# Revit family: Door-Slider-Fleetwood-3070-OXIXO
name_source: partatom
category: Doors
revit_build: Autodesk Revit Architecture 2013 (Build: 20120221_2030(x64)
units: mm (PartAtom-declared; Revit-internal decimal feet)

## types (6) — shared parameters
Analytic Construction = <None>
Configuration = OXIXO
Equal_Centerlines = Yes
Exterior Wrap Overhang = 0.5 "
Frame_&_Panel = Aluminum, Anodized Clear
Function = Exterior
Glazing = Glass
Hardware = Stainless Steel, Brushed
Height = 96 "
Interior Wrap Overhang = 0.5 "
Manufacturer = Fleetwood Windows and Doors
Model = 3070
Panel_1 = 24.2585 "
Panel_2 = 24.6933 "
Panel_3 = 24.6933 "
Panel_4 = 24.2585 "
Panel_Height = 94.4688 "
Rough Height = 96.25 "
Rough Width = 96.5 "
Thickness = 3.816 "
URL = www.fleetwoodusa.com
Wall Closure = By host
Width = 96 "
zero-valued in all types: Centerline_1, Centerline_2, Centerline_3

## per-type parameters (varying)
| type | Actuator_Height | Panel_1_Configuration | Panel_2_Configuration | Panel_3_Configuration | Panel_4_Configuration |
| Archetype Hardware_Archetype Narrow Fixed Stile | 53.75 " | 3070_EX_Panel : Fixed Panel Archetype Narrow Stile | 3070_EX_Panel : Active Lead Panel Right Archetype | 3070_EX_Panel : Archetype_Inactive_Panel | 3070_EX_Panel : Fixed Panel Archetype Narrow Stile |
| Archetype Hardware_Archetype Fixed Stile | 53.75 " | 3070_EX_Panel : Fixed Panel Archetype Stile | 3070_EX_Panel : Active Lead Panel Right Archetype | 3070_EX_Panel : Archetype_Inactive_Panel | 3070_EX_Panel : Fixed Panel Archetype Stile |
| Archetype Narrow Hardware_Narrow Fixed Stile | 46 " | 3070_EX_Panel : Fixed Panel Narrow Fixed Stile | 3070_EX_Panel : Active Lead Panel Right Archetype Narrow | 3070_EX_Panel : Archetype_Narrow_Inactive_Panel | 3070_EX_Panel : Fixed Panel Narrow Fixed Stile |
| Archetype Narrow Hardware_Archetype Narrow Fixed Stile | 46 " | 3070_EX_Panel : Fixed Panel Archetype Narrow Stile | 3070_EX_Panel : Active Lead Panel Right Archetype Narrow | 3070_EX_Panel : Archetype_Narrow_Inactive_Panel | 3070_EX_Panel : Fixed Panel Archetype Narrow Stile |
| Archetype Narrow Hardware_Archetype Fixed Stile | 46 " | 3070_EX_Panel : Fixed Panel Archetype Stile | 3070_EX_Panel : Active Lead Panel Right Archetype Narrow | 3070_EX_Panel : Archetype_Narrow_Inactive_Panel | 3070_EX_Panel : Fixed Panel Archetype Stile |
| Archetype Hardware_Narrow Fixed Stile | 53.75 " | 3070_EX_Panel : Fixed Panel Narrow Fixed Stile | 3070_EX_Panel : Active Lead Panel Right Archetype | 3070_EX_Panel : Archetype_Inactive_Panel | 3070_EX_Panel : Fixed Panel Narrow Fixed Stile |

## geometry (parser evidence)
native form markers: Blend x12, Sweep x12
no freeform markers — native parametric forms only
